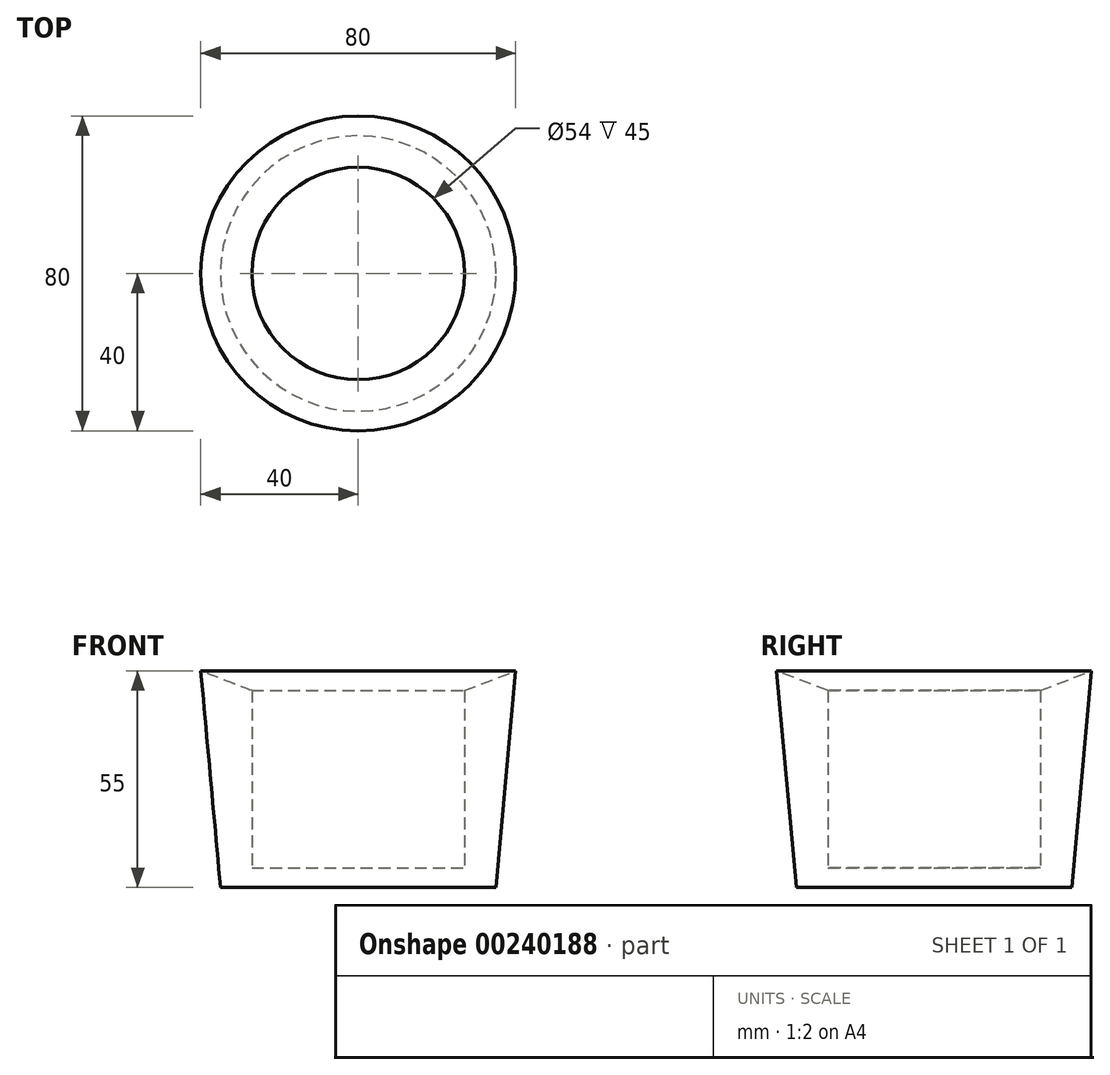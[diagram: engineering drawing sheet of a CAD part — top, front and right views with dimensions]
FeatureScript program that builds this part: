
annotation { "Feature Type Name" : "Feature", "Feature Type Description" : "" }
export const myFeature = defineFeature(function(context is Context, id is Id, definition is map)
    precondition{}
    {
        {
            var Q0;
            Q0=qCreatedBy(makeId("Right.planeOp"),FACE);
            var sketch = newSketch(context, id + "F0", { "sketchPlane" : qUnion([Q0])});
            skLineSegment(sketch, "E0", {"start": v(-40, 55) * mm, "end": v(-35, 0) * mm});
            skLineSegment(sketch, "E1", {"start": v(-35, 0) * mm, "end": v(0, 0) * mm});
            skLineSegment(sketch, "E2", {"start": v(0, 0) * mm, "end": v(0, 5) * mm});
            skLineSegment(sketch, "E3", {"start": v(0, 5) * mm, "end": v(-27, 5) * mm});
            skLineSegment(sketch, "E4", {"start": v(-27, 5) * mm, "end": v(-27, 50) * mm});
            skLineSegment(sketch, "E5", {"start": v(-27, 50) * mm, "end": v(-40, 55) * mm});
            skSolve(sketch);
        }
        {
            var Q0;
            Q0=makeQuery(id+"F0.imprint","IMPRINT",FACE,{"disambiguationData":[TD([[makeQuery(id+"F0.imprint","IMPRINT",EDGE,{"derivedFrom":sQuery(id+"F0.wireOp",EDGE,"E0")}),1.0]])]});
            var Q1;
            Q1=sQuery(id+"F0.wireOp",EDGE,"E2");
            revolve(context, id + "F1", {"entities" : qUnion([Q0]), "axis" : qUnion([Q1]), "revolveType" : RevolveType.FULL});
        }
    });
